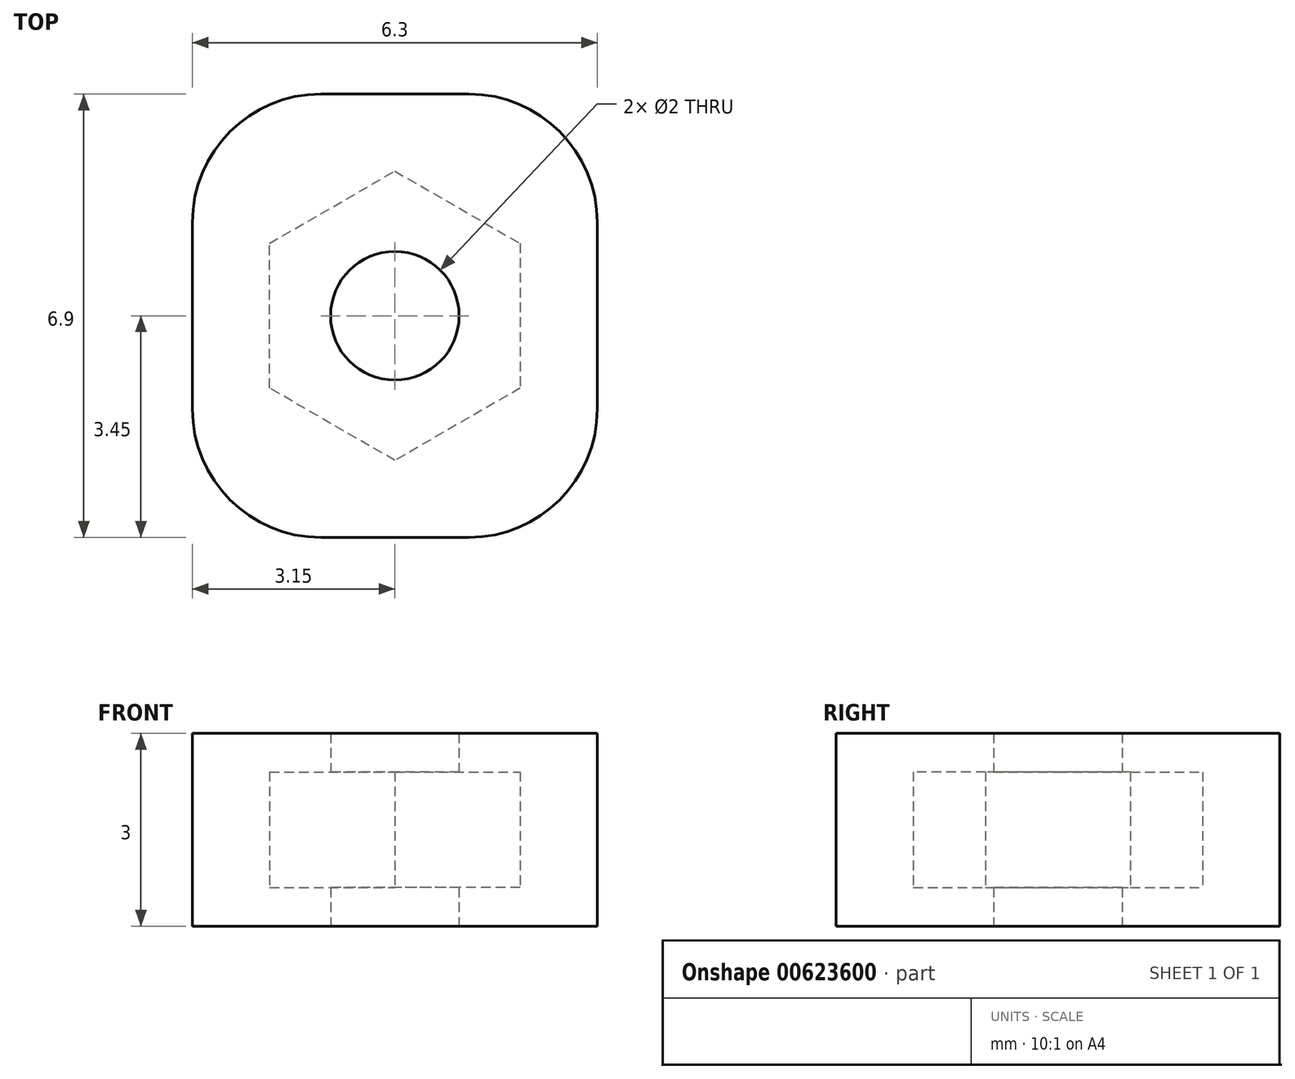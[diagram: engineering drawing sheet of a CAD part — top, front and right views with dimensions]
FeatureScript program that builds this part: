
annotation { "Feature Type Name" : "Feature", "Feature Type Description" : "" }
export const myFeature = defineFeature(function(context is Context, id is Id, definition is map)
    precondition{}
    {
        {
            var Q0;
            Q0=qCreatedBy(makeId("Top.planeOp"),FACE);
            var sketch = newSketch(context, id + "F0", { "sketchPlane" : qUnion([Q0])});
            skLineSegment(sketch, "E0.bottom", {"start": v(3.15, 3.45) * mm, "end": v(-3.15, 3.45) * mm});
            skLineSegment(sketch, "E0.top", {"start": v(3.15, -3.45) * mm, "end": v(-3.15, -3.45) * mm});
            skLineSegment(sketch, "E0.left", {"start": v(3.15, 3.45) * mm, "end": v(3.15, -3.45) * mm});
            skLineSegment(sketch, "E0.right", {"start": v(-3.15, 3.45) * mm, "end": v(-3.15, -3.45) * mm});
            skPoint(sketch, "E0.middle", {"position": v(0, 0) * mm});
            skCircle(sketch, "E1.cCircle", {"center": v(0, 0) * mm, "radius": 1.95 * mm, "construction": true});
            skLineSegment(sketch, "E1.0", {"start": v(0, 2.25) * mm, "end": v(1.95, 1.13) * mm, "construction": true});
            skLineSegment(sketch, "E1.1", {"start": v(1.95, 1.13) * mm, "end": v(1.95, -1.13) * mm, "construction": true});
            skLineSegment(sketch, "E1.2", {"start": v(1.95, -1.13) * mm, "end": v(0, -2.25) * mm, "construction": true});
            skLineSegment(sketch, "E1.3", {"start": v(0, -2.25) * mm, "end": v(-1.95, -1.13) * mm, "construction": true});
            skLineSegment(sketch, "E1.4", {"start": v(-1.95, -1.13) * mm, "end": v(-1.95, 1.13) * mm, "construction": true});
            skLineSegment(sketch, "E1.5", {"start": v(-1.95, 1.13) * mm, "end": v(0, 2.25) * mm, "construction": true});
            skPoint(sketch, "E1.0.midPoint", {"position": v(0.98, 1.69) * mm});
            skCircle(sketch, "E2", {"center": v(0, 0) * mm, "radius": 1 * mm});
            skSolve(sketch);
        }
        {
            var Q0;
            Q0 = qSketchRegion(id + "F0", true);
            extrude(context, id + "F1", {"entities" : qUnion([Q0]), "depth" : .6 * mm, "offsetDistance" : 25 * mm});
        }
        {
            var Q0;
            Q0=makeQuery(id+"F1.opExtrude","CAP_FACE",FACE,{"disambiguationData":[OSD([sQuery(id+"F0.wireOp",EDGE,"E0.bottom"),sQuery(id+"F0.wireOp",EDGE,"E0.top"),sQuery(id+"F0.wireOp",EDGE,"E0.left"),sQuery(id+"F0.wireOp",EDGE,"E0.right"),sQuery(id+"F0.wireOp",EDGE,"E2")])],"isStart":false});
            var sketch = newSketch(context, id + "F2", { "sketchPlane" : qUnion([Q0])});
            skLineSegment(sketch, "E3.0", {"start": v(3.15, 3.45) * mm, "end": v(-3.15, 3.45) * mm});
            skLineSegment(sketch, "E4.0", {"start": v(-3.15, 3.45) * mm, "end": v(-3.15, -3.45) * mm});
            skLineSegment(sketch, "E5.0", {"start": v(3.15, -3.45) * mm, "end": v(-3.15, -3.45) * mm});
            skLineSegment(sketch, "E6.0", {"start": v(3.15, 3.45) * mm, "end": v(3.15, -3.45) * mm});
            skLineSegment(sketch, "E7.0", {"start": v(0, 2.25) * mm, "end": v(1.95, 1.13) * mm});
            skLineSegment(sketch, "E8.0", {"start": v(1.95, 1.13) * mm, "end": v(1.95, -1.13) * mm});
            skLineSegment(sketch, "E9.0", {"start": v(1.95, -1.13) * mm, "end": v(0, -2.25) * mm});
            skLineSegment(sketch, "E10.0", {"start": v(0, -2.25) * mm, "end": v(-1.95, -1.13) * mm});
            skLineSegment(sketch, "E11.0", {"start": v(-1.95, -1.13) * mm, "end": v(-1.95, 1.13) * mm});
            skLineSegment(sketch, "E12.0", {"start": v(-1.95, 1.13) * mm, "end": v(0, 2.25) * mm});
            skSolve(sketch);
        }
        {
            var Q0;
            Q0 = qSketchRegion(id + "F2", true);
            extrude(context, id + "F3", {"entities" : qUnion([Q0]), "operationType" : NewBodyOperationType.ADD, "depth" : 1.8 * mm, "offsetDistance" : 25 * mm});
        }
        {
            var Q0;
            Q0=makeQuery(id+"F3.opExtrude","CAP_FACE",FACE,{"disambiguationData":[OSD([sQuery(id+"F2.wireOp",EDGE,"E3.0"),sQuery(id+"F2.wireOp",EDGE,"E4.0"),sQuery(id+"F2.wireOp",EDGE,"E5.0"),sQuery(id+"F2.wireOp",EDGE,"E6.0"),sQuery(id+"F2.wireOp",EDGE,"E7.0"),sQuery(id+"F2.wireOp",EDGE,"E8.0"),sQuery(id+"F2.wireOp",EDGE,"E9.0"),sQuery(id+"F2.wireOp",EDGE,"E10.0"),sQuery(id+"F2.wireOp",EDGE,"E11.0"),sQuery(id+"F2.wireOp",EDGE,"E12.0")])],"isStart":false});
            var sketch = newSketch(context, id + "F4", { "sketchPlane" : qUnion([Q0])});
            skLineSegment(sketch, "E13.0", {"start": v(3.15, 3.45) * mm, "end": v(-3.15, 3.45) * mm});
            skLineSegment(sketch, "E14.0", {"start": v(-3.15, 3.45) * mm, "end": v(-3.15, -3.45) * mm});
            skLineSegment(sketch, "E15.0", {"start": v(3.15, -3.45) * mm, "end": v(-3.15, -3.45) * mm});
            skLineSegment(sketch, "E16.0", {"start": v(3.15, 3.45) * mm, "end": v(3.15, -3.45) * mm});
            skCircle(sketch, "E17.0", {"center": v(0, 0) * mm, "radius": 1 * mm});
            skSolve(sketch);
        }
        {
            var Q0;
            Q0 = qSketchRegion(id + "F4", true);
            extrude(context, id + "F5", {"entities" : qUnion([Q0]), "operationType" : NewBodyOperationType.ADD, "depth" : .6 * mm, "offsetDistance" : 25 * mm});
        }
        {
            var Q0;
            Q0=makeQuery(id+"F5.boolean.opBoolean","MERGE",EDGE,{"derivedFrom":[makeQuery(id+"F3.boolean.opBoolean","MERGE",EDGE,{"derivedFrom":[makeQuery(id+"F1.opExtrude","SWEPT_EDGE",EDGE,{"disambiguationData":[OSD([sQuery(id+"F0.wireOp",EDGE,"E0.top"),sQuery(id+"F0.wireOp",EDGE,"E0.left")])]}),makeQuery(id+"F3.opExtrude","SWEPT_EDGE",EDGE,{"disambiguationData":[OSD([sQuery(id+"F2.wireOp",EDGE,"E5.0"),sQuery(id+"F2.wireOp",EDGE,"E6.0")])]})]}),makeQuery(id+"F5.opExtrude","SWEPT_EDGE",EDGE,{"disambiguationData":[OSD([sQuery(id+"F4.wireOp",EDGE,"E15.0"),sQuery(id+"F4.wireOp",EDGE,"E16.0")])]})]});
            var Q1;
            Q1=makeQuery(id+"F5.boolean.opBoolean","MERGE",EDGE,{"derivedFrom":[makeQuery(id+"F3.boolean.opBoolean","MERGE",EDGE,{"derivedFrom":[makeQuery(id+"F1.opExtrude","SWEPT_EDGE",EDGE,{"disambiguationData":[OSD([sQuery(id+"F0.wireOp",EDGE,"E0.bottom"),sQuery(id+"F0.wireOp",EDGE,"E0.left")])]}),makeQuery(id+"F3.opExtrude","SWEPT_EDGE",EDGE,{"disambiguationData":[OSD([sQuery(id+"F2.wireOp",EDGE,"E3.0"),sQuery(id+"F2.wireOp",EDGE,"E6.0")])]})]}),makeQuery(id+"F5.opExtrude","SWEPT_EDGE",EDGE,{"disambiguationData":[OSD([sQuery(id+"F4.wireOp",EDGE,"E13.0"),sQuery(id+"F4.wireOp",EDGE,"E16.0")])]})]});
            var Q2;
            Q2=makeQuery(id+"F5.boolean.opBoolean","MERGE",EDGE,{"derivedFrom":[makeQuery(id+"F3.boolean.opBoolean","MERGE",EDGE,{"derivedFrom":[makeQuery(id+"F1.opExtrude","SWEPT_EDGE",EDGE,{"disambiguationData":[OSD([sQuery(id+"F0.wireOp",EDGE,"E0.bottom"),sQuery(id+"F0.wireOp",EDGE,"E0.right")])]}),makeQuery(id+"F3.opExtrude","SWEPT_EDGE",EDGE,{"disambiguationData":[OSD([sQuery(id+"F2.wireOp",EDGE,"E3.0"),sQuery(id+"F2.wireOp",EDGE,"E4.0")])]})]}),makeQuery(id+"F5.opExtrude","SWEPT_EDGE",EDGE,{"disambiguationData":[OSD([sQuery(id+"F4.wireOp",EDGE,"E13.0"),sQuery(id+"F4.wireOp",EDGE,"E14.0")])]})]});
            var Q3;
            Q3=makeQuery(id+"F5.boolean.opBoolean","MERGE",EDGE,{"derivedFrom":[makeQuery(id+"F3.boolean.opBoolean","MERGE",EDGE,{"derivedFrom":[makeQuery(id+"F1.opExtrude","SWEPT_EDGE",EDGE,{"disambiguationData":[OSD([sQuery(id+"F0.wireOp",EDGE,"E0.top"),sQuery(id+"F0.wireOp",EDGE,"E0.right")])]}),makeQuery(id+"F3.opExtrude","SWEPT_EDGE",EDGE,{"disambiguationData":[OSD([sQuery(id+"F2.wireOp",EDGE,"E4.0"),sQuery(id+"F2.wireOp",EDGE,"E5.0")])]})]}),makeQuery(id+"F5.opExtrude","SWEPT_EDGE",EDGE,{"disambiguationData":[OSD([sQuery(id+"F4.wireOp",EDGE,"E14.0"),sQuery(id+"F4.wireOp",EDGE,"E15.0")])]})]});
            fillet(context, id + "F6", {"entities" : qUnion([Q0, Q1, Q2, Q3]), "radius" : 2 * mm, "tangentPropagation" : true, "allowEdgeOverflow" : false});
        }
    });
